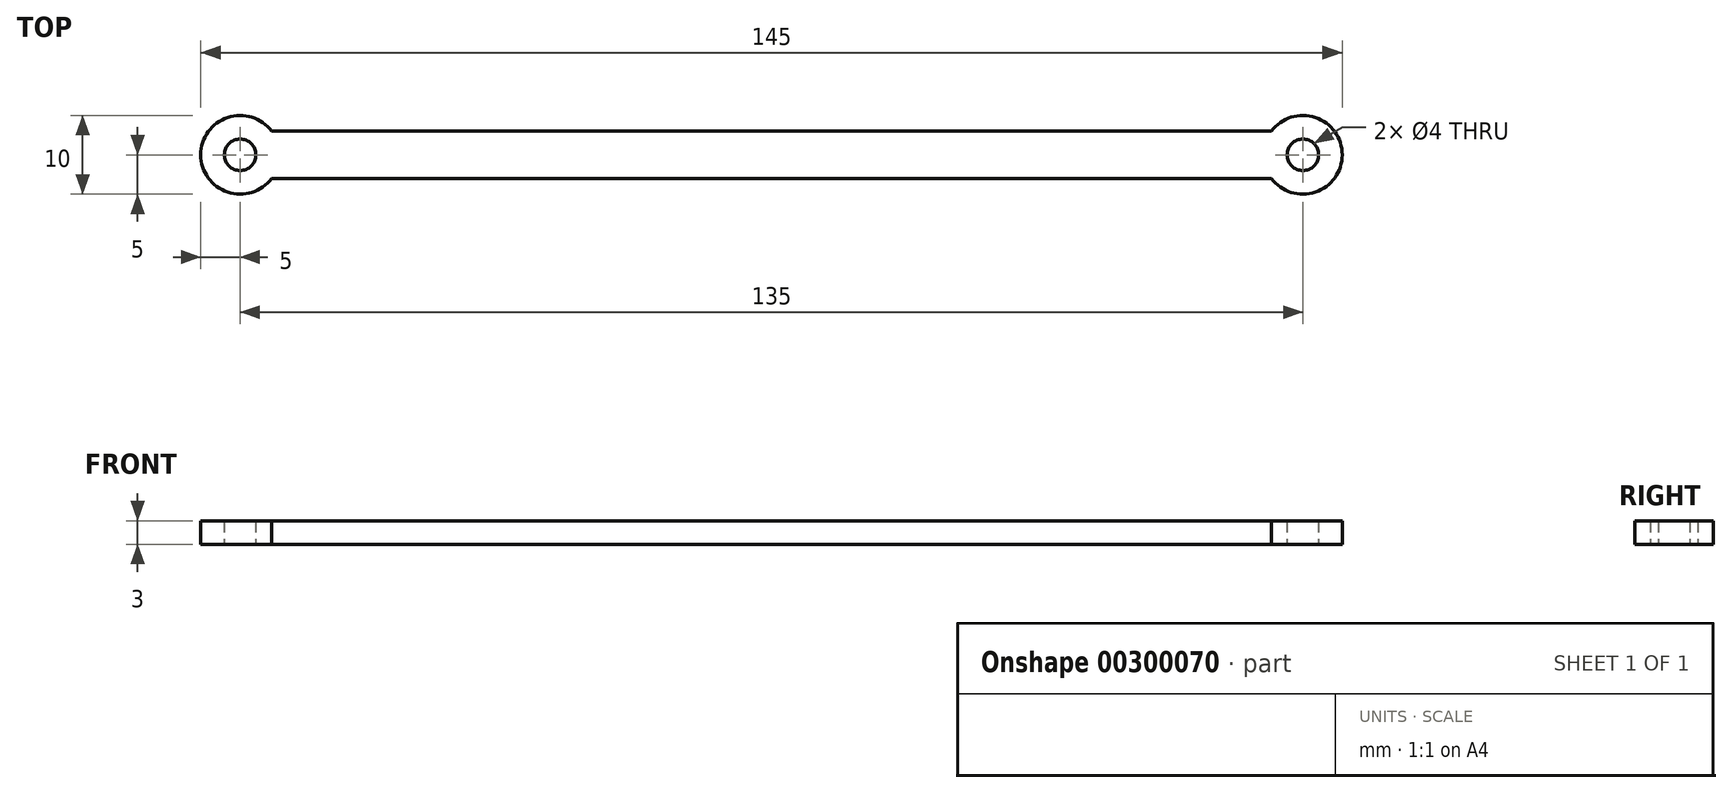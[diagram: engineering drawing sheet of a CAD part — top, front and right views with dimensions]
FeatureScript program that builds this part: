
annotation { "Feature Type Name" : "Feature", "Feature Type Description" : "" }
export const myFeature = defineFeature(function(context is Context, id is Id, definition is map)
    precondition{}
    {
        {
            var Q0;
            Q0=qCreatedBy(makeId("Top.planeOp"),FACE);
            var sketch = newSketch(context, id + "F0", { "sketchPlane" : qUnion([Q0])});
            skArc(sketch, "E0", {"start": v(-63.5, 3) * mm, "mid": v(-72.5, 0) * mm, "end": v(-63.5, -3) * mm});
            skArc(sketch, "E1", {"start": v(63.5, -3) * mm, "mid": v(72.5, 0) * mm, "end": v(63.5, 3) * mm});
            skLineSegment(sketch, "E2", {"start": v(-63.5, 3) * mm, "end": v(63.5, 3) * mm});
            skLineSegment(sketch, "E3", {"start": v(-63.5, -3) * mm, "end": v(63.5, -3) * mm});
            skSolve(sketch);
        }
        {
            var Q0;
            Q0 = qSketchRegion(id + "F0", true);
            extrude(context, id + "F1", {"entities" : qUnion([Q0]), "depth" : 3 * mm});
        }
        {
            var Q0;
            Q0=qCreatedBy(makeId("Top.planeOp"),FACE);
            var sketch = newSketch(context, id + "F2", { "sketchPlane" : qUnion([Q0])});
            skCircle(sketch, "E4", {"center": v(67.5, 0) * mm, "radius": 2 * mm});
            skCircle(sketch, "E5", {"center": v(-67.5, 0) * mm, "radius": 2 * mm});
            skSolve(sketch);
        }
        {
            var Q0;
            Q0 = qSketchRegion(id + "F2", true);
            extrude(context, id + "F3", {"entities" : qUnion([Q0]), "operationType" : NewBodyOperationType.REMOVE, "depth" : 25 * mm});
        }
    });
